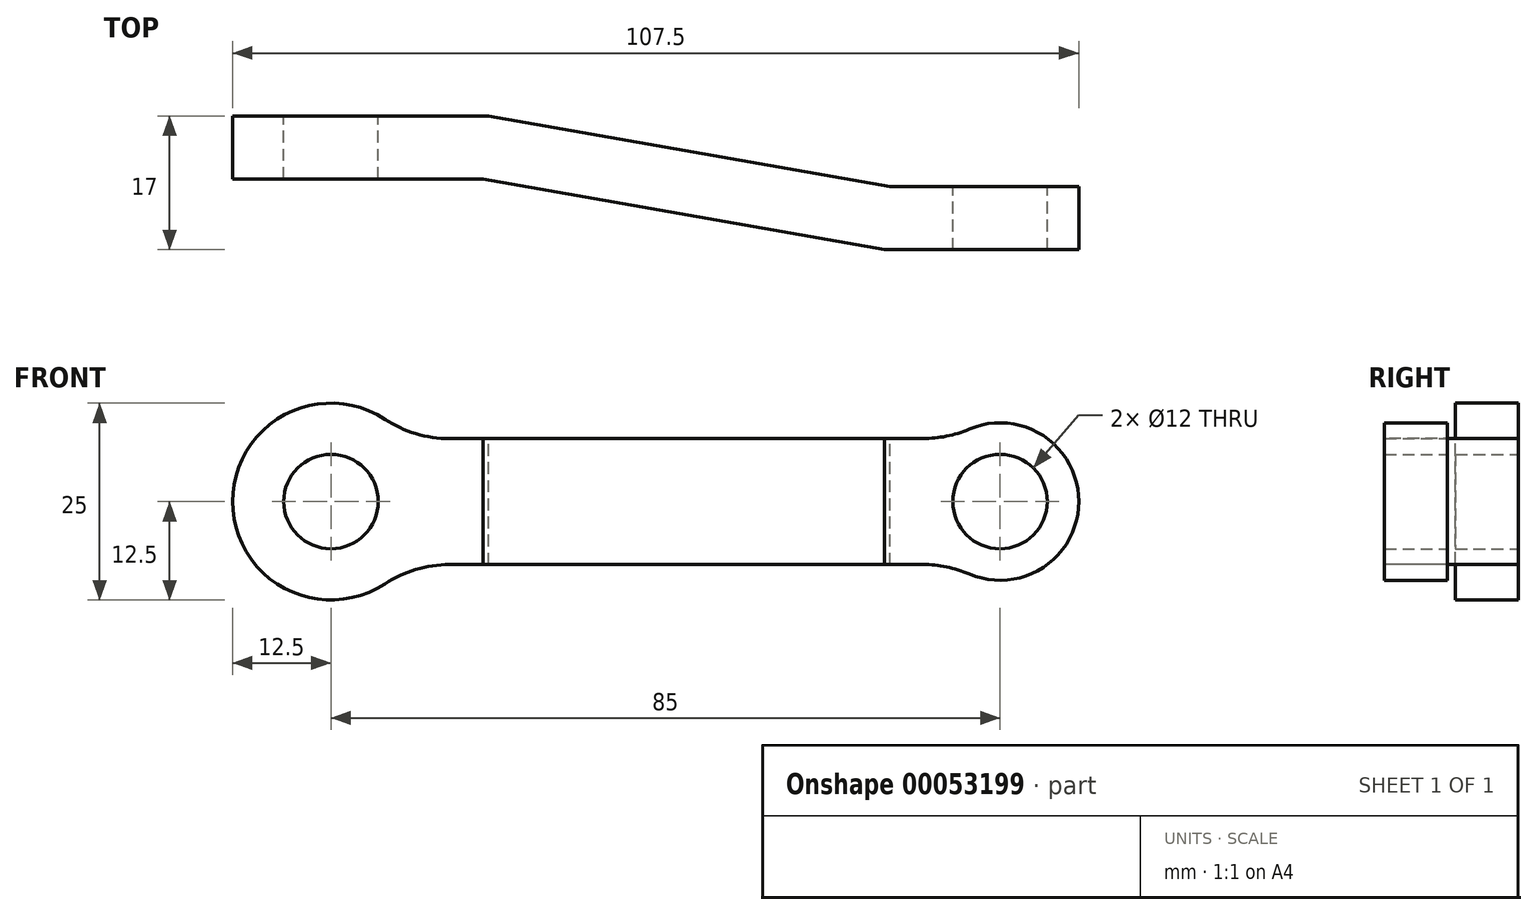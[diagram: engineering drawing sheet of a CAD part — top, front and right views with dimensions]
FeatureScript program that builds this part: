
annotation { "Feature Type Name" : "Feature", "Feature Type Description" : "" }
export const myFeature = defineFeature(function(context is Context, id is Id, definition is map)
    precondition{}
    {
        {
            var Q0;
            Q0=qCreatedBy(makeId("Front.planeOp"),FACE);
            var sketch = newSketch(context, id + "F0", { "sketchPlane" : qUnion([Q0])});
            skCircle(sketch, "E0", {"center": v(0, 0) * mm, "radius": 12.5 * mm});
            skCircle(sketch, "E1", {"center": v(85, 0) * mm, "radius": 10 * mm});
            skLineSegment(sketch, "E2", {"start": v(12.33, 0) * mm, "end": v(85, 0) * mm, "construction": true});
            skLineSegment(sketch, "E3", {"start": v(9.6, 8) * mm, "end": v(79, 8) * mm});
            skLineSegment(sketch, "E4.MirrorCS", {"start": v(9.6, -8) * mm, "end": v(79, -8) * mm});
            skCircle(sketch, "E5", {"center": v(0, 0) * mm, "radius": 6 * mm});
            skCircle(sketch, "E6", {"center": v(85, 0) * mm, "radius": 6 * mm});
            skSolve(sketch);
        }
        {
            var Q0;
            Q0 = qSketchRegion(id + "F0", true);
            extrude(context, id + "F1", {"entities" : qUnion([Q0]), "depth" : 25 * mm});
        }
        {
            var Q0;
            Q0=qCreatedBy(makeId("Top.planeOp"),FACE);
            var sketch = newSketch(context, id + "F2", { "sketchPlane" : qUnion([Q0])});
            skLineSegment(sketch, "E7", {"start": v(0, 0) * mm, "end": v(-12.5, 0) * mm});
            skLineSegment(sketch, "E8", {"start": v(0, 0) * mm, "end": v(20, 0) * mm});
            skLineSegment(sketch, "E9", {"start": v(20, 0) * mm, "end": v(71.04, -9) * mm});
            skLineSegment(sketch, "E10", {"start": v(71.04, -9) * mm, "end": v(95, -9) * mm});
            skLineSegment(sketch, "E11.0", {"start": v(70.34, -17) * mm, "end": v(95, -17) * mm});
            skLineSegment(sketch, "E11.1", {"start": v(19.3, -8) * mm, "end": v(70.34, -17) * mm});
            skLineSegment(sketch, "E11.2", {"start": v(0, -8) * mm, "end": v(19.3, -8) * mm});
            skLineSegment(sketch, "E11.3", {"start": v(0, -8) * mm, "end": v(-12.5, -8) * mm});
            skLineSegment(sketch, "E12", {"start": v(95, -9) * mm, "end": v(95, -17) * mm});
            skLineSegment(sketch, "E13", {"start": v(-12.5, 0) * mm, "end": v(-12.5, -8) * mm});
            skLineSegment(sketch, "E14", {"start": v(95, 0) * mm, "end": v(95, -25) * mm});
            skLineSegment(sketch, "E15", {"start": v(-12.5, -25) * mm, "end": v(-12.5, 0) * mm});
            skSolve(sketch);
        }
        {
            var Q0;
            Q0 = qSketchRegion(id + "F2", true);
            extrude(context, id + "F3", {"entities" : qUnion([Q0]), "operationType" : NewBodyOperationType.INTERSECT, "endBound" : BoundingType.SYMMETRIC, "oppositeDirection" : true, "depth" : 25.4 * mm});
        }
        {
            var Q0;
            Q0=makeQuery(id+"F1.opExtrude","SWEPT_EDGE",EDGE,{"disambiguationData":[OSD([sQuery(id+"F0.wireOp",EDGE,"E1"),sQuery(id+"F0.wireOp",EDGE,"E3")])]});
            fillet(context, id + "F4", {"entities" : qUnion([Q0]), "radius" : 15 * mm, "tangentPropagation" : true, "allowEdgeOverflow" : false});
        }
        {
            var Q0;
            Q0=makeQuery(id+"F1.opExtrude","SWEPT_EDGE",EDGE,{"disambiguationData":[OSD([sQuery(id+"F0.wireOp",EDGE,"E0"),sQuery(id+"F0.wireOp",EDGE,"E3")])]});
            var Q1;
            Q1=makeQuery(id+"F1.opExtrude","SWEPT_EDGE",EDGE,{"disambiguationData":[OSD([sQuery(id+"F0.wireOp",EDGE,"E0"),sQuery(id+"F0.wireOp",EDGE,"E4.MirrorCS")])]});
            var Q2;
            Q2=makeQuery(id+"F1.opExtrude","SWEPT_EDGE",EDGE,{"disambiguationData":[OSD([sQuery(id+"F0.wireOp",EDGE,"E1"),sQuery(id+"F0.wireOp",EDGE,"E4.MirrorCS")])]});
            fillet(context, id + "F5", {"entities" : qUnion([Q0, Q1, Q2]), "radius" : 15 * mm, "tangentPropagation" : true, "allowEdgeOverflow" : false});
        }
    });
